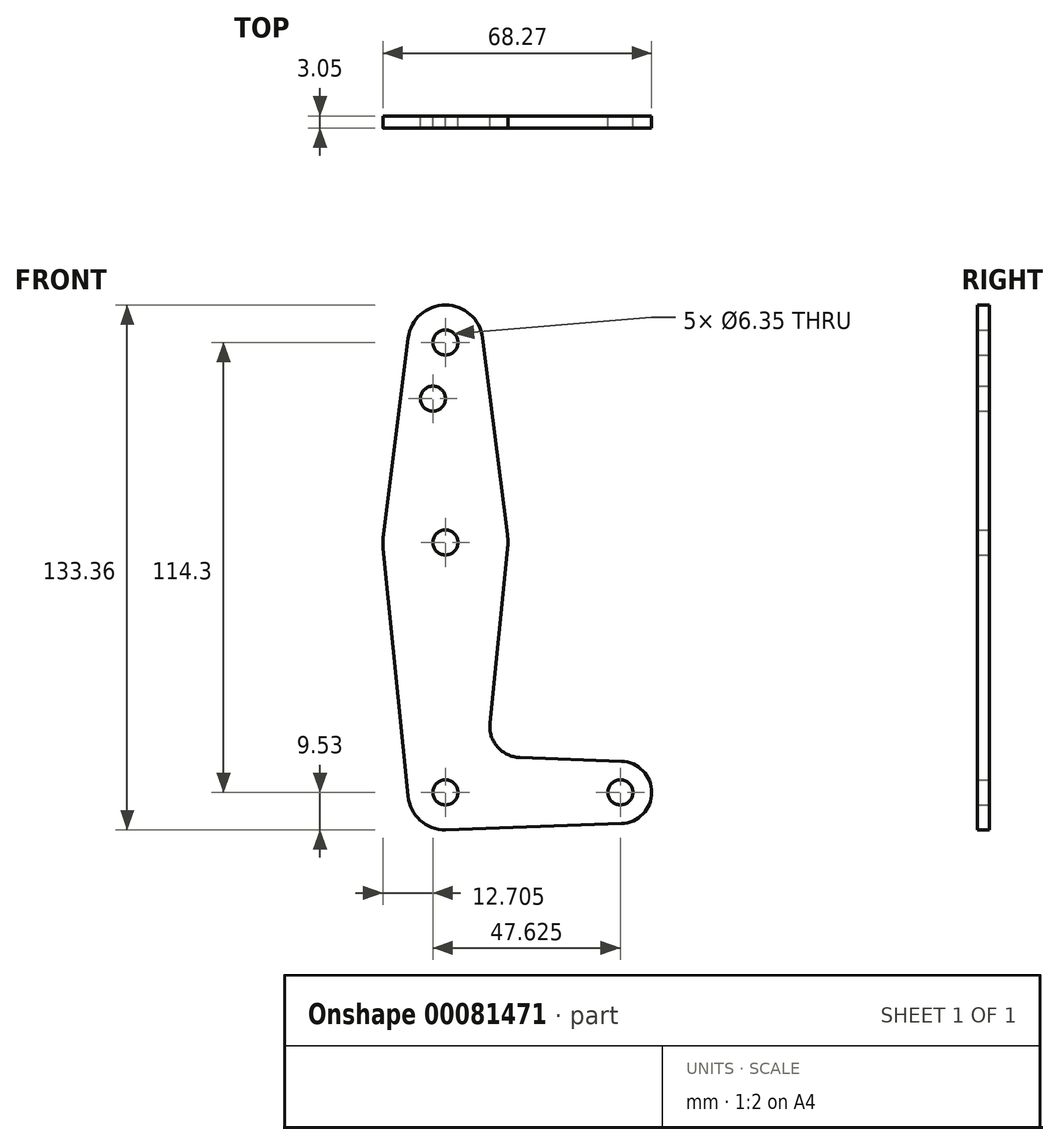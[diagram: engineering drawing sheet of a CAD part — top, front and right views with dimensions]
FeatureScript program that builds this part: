
annotation { "Feature Type Name" : "Feature", "Feature Type Description" : "" }
export const myFeature = defineFeature(function(context is Context, id is Id, definition is map)
    precondition{}
    {
        {
            var Q0;
            Q0=qCreatedBy(makeId("Front.planeOp"),FACE);
            var sketch = newSketch(context, id + "F0", { "sketchPlane" : qUnion([Q0])});
            skLineSegment(sketch, "E0", {"start": v(0, 0) * mm, "end": v(0, 114.3) * mm, "construction": true});
            skLineSegment(sketch, "E1", {"start": v(0, 0) * mm, "end": v(44.45, 0) * mm, "construction": true});
            skCircle(sketch, "E2", {"center": v(0, 114.3) * mm, "radius": 9.53 * mm});
            skCircle(sketch, "E3", {"center": v(0, 63.5) * mm, "radius": 15.88 * mm});
            skCircle(sketch, "E4", {"center": v(0, 0) * mm, "radius": 9.53 * mm});
            skCircle(sketch, "E5", {"center": v(44.45, 0) * mm, "radius": 7.94 * mm});
            skLineSegment(sketch, "E6", {"start": v(-9.45, 115.5) * mm, "end": v(-15.75, 65.48) * mm});
            skLineSegment(sketch, "E7", {"start": v(9.45, 115.5) * mm, "end": v(15.75, 65.48) * mm});
            skLineSegment(sketch, "E8", {"start": v(15.8, 61.9) * mm, "end": v(11.3, 17.6) * mm});
            skLineSegment(sketch, "E9", {"start": v(18.93, 8.85) * mm, "end": v(44.73, 7.93) * mm});
            skLineSegment(sketch, "E10", {"start": v(0, -9.52) * mm, "end": v(44.73, -7.93) * mm});
            skLineSegment(sketch, "E11", {"start": v(-15.8, 61.91) * mm, "end": v(-9.48, -0.95) * mm});
            skArc(sketch, "E12.filletArc", {"start": v(11.3, 17.6) * mm, "mid": v(13.22, 11.57) * mm, "end": v(18.93, 8.85) * mm});
            skPoint(sketch, "E13.centerSnap0", {"position": v(-12.6, 90.49) * mm});
            skCircle(sketch, "E14", {"center": v(-3.18, 100.03) * mm, "radius": 3.18 * mm});
            skCircle(sketch, "E15", {"center": v(0, 114.3) * mm, "radius": 3.18 * mm});
            skCircle(sketch, "E16", {"center": v(0, 63.5) * mm, "radius": 3.18 * mm});
            skCircle(sketch, "E17", {"center": v(0, 0) * mm, "radius": 3.18 * mm});
            skCircle(sketch, "E18", {"center": v(44.45, 0) * mm, "radius": 3.18 * mm});
            skSolve(sketch);
        }
        {
            var Q0;
            Q0=makeQuery(id+"F0.imprint","IMPRINT",FACE,{"disambiguationData":[TD([[makeQuery(id+"F0.imprint","IMPRINT",EDGE,{"derivedFrom":sQuery(id+"F0.wireOp",EDGE,"E15")}),-1.0]])]});
            var Q1;
            {var subQ1=sQuery(id+"F0.wireOp",EDGE,"E6");Q1=makeQuery(id+"F0.imprint","IMPRINT",FACE,{"disambiguationData":[TD([[makeQuery(id+"F0.imprint","IMPRINT",EDGE,{"derivedFrom":subQ1}),1.0]])]});}
            var Q2;
            Q2=makeQuery(id+"F0.imprint","IMPRINT",FACE,{"disambiguationData":[TD([[makeQuery(id+"F0.imprint","IMPRINT",EDGE,{"derivedFrom":sQuery(id+"F0.wireOp",EDGE,"E16")}),-1.0]])]});
            var Q3;
            {var subQ0=sQuery(id+"F0.wireOp",EDGE,"E8");Q3=makeQuery(id+"F0.imprint","IMPRINT",FACE,{"disambiguationData":[TD([[makeQuery(id+"F0.imprint","IMPRINT",EDGE,{"derivedFrom":subQ0}),-1.0]])]});}
            var Q4;
            Q4=makeQuery(id+"F0.imprint","IMPRINT",FACE,{"disambiguationData":[TD([[makeQuery(id+"F0.imprint","IMPRINT",EDGE,{"derivedFrom":sQuery(id+"F0.wireOp",EDGE,"E17")}),-1.0]])]});
            var Q5;
            Q5=makeQuery(id+"F0.imprint","IMPRINT",FACE,{"disambiguationData":[TD([[makeQuery(id+"F0.imprint","IMPRINT",EDGE,{"derivedFrom":sQuery(id+"F0.wireOp",EDGE,"E18")}),-1.0]])]});
            extrude(context, id + "F1", {"entities" : qUnion([Q0, Q1, Q2, Q3, Q4, Q5]), "depth" : 3.05 * mm});
        }
    });
